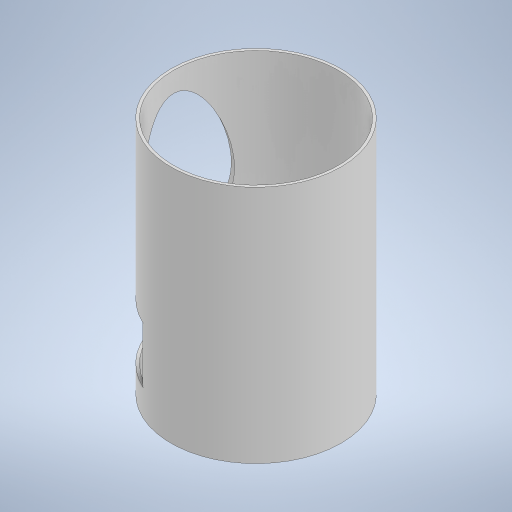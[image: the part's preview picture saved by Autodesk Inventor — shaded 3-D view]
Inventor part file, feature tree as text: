
AUTODESK INVENTOR PART (.ipt)
format: ipt  version: 2024.3 (Build 283343000, 343)  size: 246,784 bytes
history: native  units: mm
features: sketch x4, extrude x3, plane x1
ambient origin geometry x8: Origin, YZ Plane, XZ Plane, XY Plane, X Axis, Y Axis, Z Axis, Center Point
bodies: Solid1 (feature_tree)
feature tree (8):
  extrude  "Extrusion1"  Depth=128.0mm
  extrude  "Extrusion2"  Depth=42.0mm
  sketch  "Sketch3"  dims[d5=116.0mm d6=20.0mm]
  plane  "Work Plane1"
  extrude  "Extrusion3"  Depth=20.0mm
  sketch  "Sketch1"  dims[d0=2.0mm d1=128.0mm]
  sketch  "Sketch2"  dims[d2=180.0mm d3=0.0mm d4=42.0mm]
  sketch  "Sketch4"  dims[d7=58.0mm d8=0.0mm d9=0.0mm d10=110.0mm d11=135.0deg d12=70.0mm d13=0.0mm d14=0.0mm d15=40.0mm]
